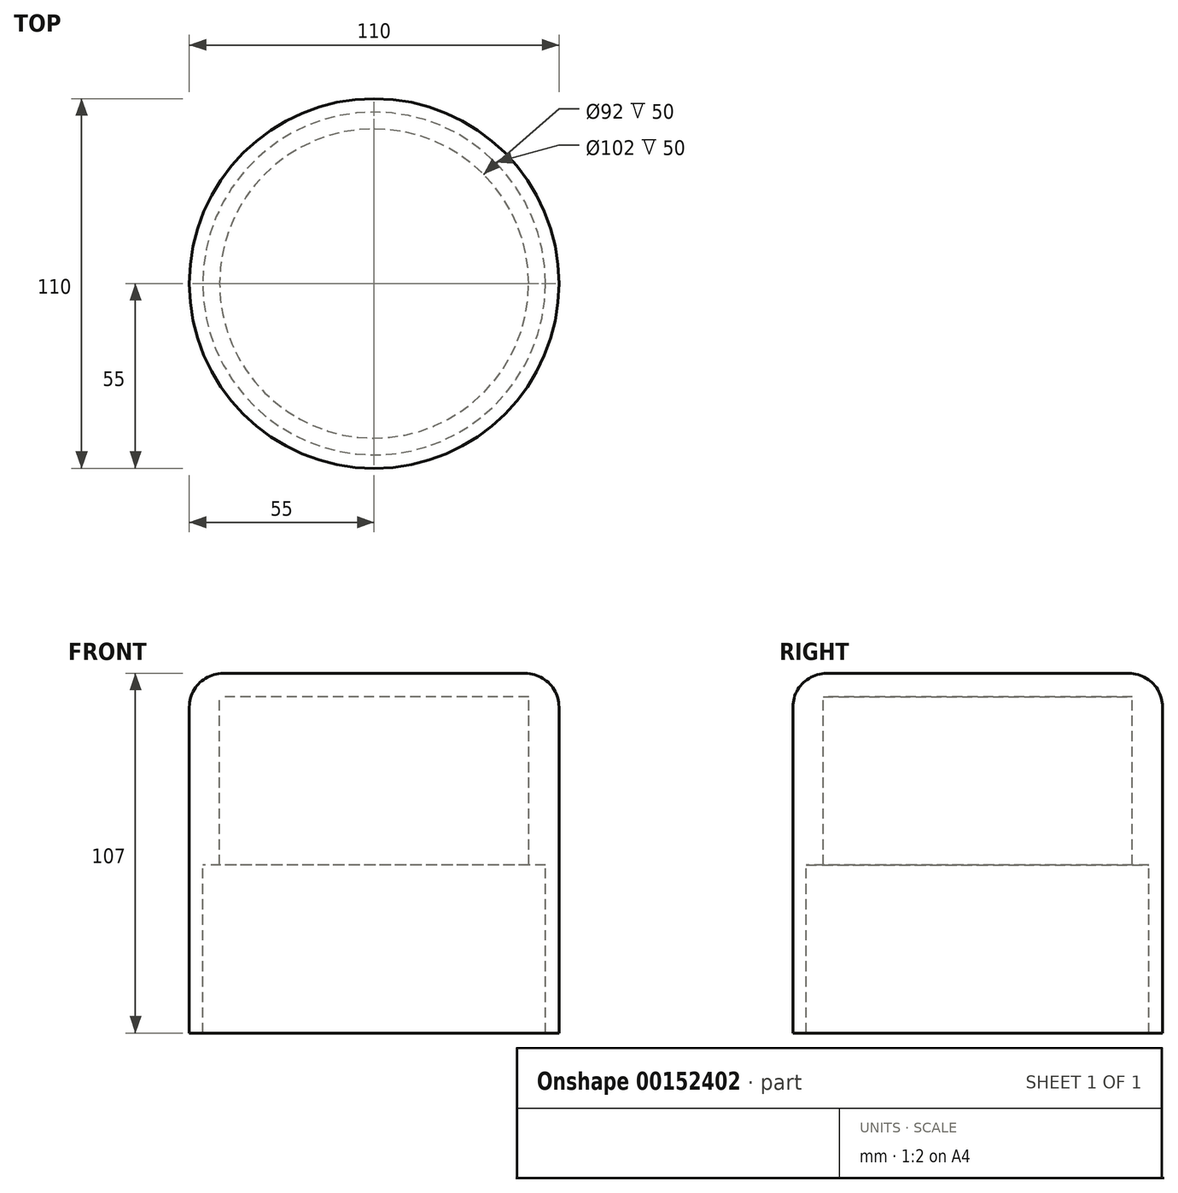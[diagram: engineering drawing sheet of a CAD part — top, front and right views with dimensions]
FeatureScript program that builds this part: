
annotation { "Feature Type Name" : "Feature", "Feature Type Description" : "" }
export const myFeature = defineFeature(function(context is Context, id is Id, definition is map)
    precondition{}
    {
        {
            var Q0;
            Q0=qCreatedBy(makeId("Top.planeOp"),FACE);
            var sketch = newSketch(context, id + "F0", { "sketchPlane" : qUnion([Q0])});
            skCircle(sketch, "E0", {"center": v(0, 0) * mm, "radius": 55 * mm});
            skCircle(sketch, "E1", {"center": v(0, 0) * mm, "radius": 51 * mm});
            skCircle(sketch, "E2", {"center": v(0, 0) * mm, "radius": 46 * mm});
            skSolve(sketch);
        }
        {
            var Q0;
            Q0=makeQuery(id+"F0.imprint","IMPRINT",FACE,{"disambiguationData":[TD([[makeQuery(id+"F0.imprint","IMPRINT",EDGE,{"derivedFrom":sQuery(id+"F0.wireOp",EDGE,"E0")}),1.0]])]});
            var Q1;
            Q1=makeQuery(id+"F0.imprint","IMPRINT",FACE,{"disambiguationData":[TD([[makeQuery(id+"F0.imprint","IMPRINT",EDGE,{"derivedFrom":sQuery(id+"F0.wireOp",EDGE,"E1")}),1.0]])]});
            var Q2;
            Q2=makeQuery(id+"F0.imprint","IMPRINT",FACE,{"disambiguationData":[TD([[makeQuery(id+"F0.imprint","IMPRINT",EDGE,{"derivedFrom":sQuery(id+"F0.wireOp",EDGE,"E2")}),1.0]])]});
            extrude(context, id + "F1", {"entities" : qUnion([Q0, Q1, Q2]), "depth" : 7 * mm});
        }
        {
            var Q0;
            Q0=makeQuery(id+"F0.imprint","IMPRINT",FACE,{"disambiguationData":[TD([[makeQuery(id+"F0.imprint","IMPRINT",EDGE,{"derivedFrom":sQuery(id+"F0.wireOp",EDGE,"E1")}),1.0]])]});
            extrude(context, id + "F2", {"entities" : qUnion([Q0]), "operationType" : NewBodyOperationType.ADD, "oppositeDirection" : true, "depth" : 50 * mm});
        }
        {
            var Q0;
            Q0=qSketchRegion(id+"F0",true);
            extrude(context, id + "F3", {"entities" : qUnion([Q0]), "operationType" : NewBodyOperationType.ADD, "oppositeDirection" : true, "depth" : 100 * mm});
        }
        {
            var Q0;
            Q0=makeQuery(id+"F1.opExtrude","CAP_EDGE",EDGE,{"disambiguationData":[OSD([sQuery(id+"F0.wireOp",EDGE,"E0")])],"isStart":false});
            fillet(context, id + "F4", {"entities" : qUnion([Q0]), "radius" : 10 * mm, "tangentPropagation" : true, "allowEdgeOverflow" : false});
        }
    });
